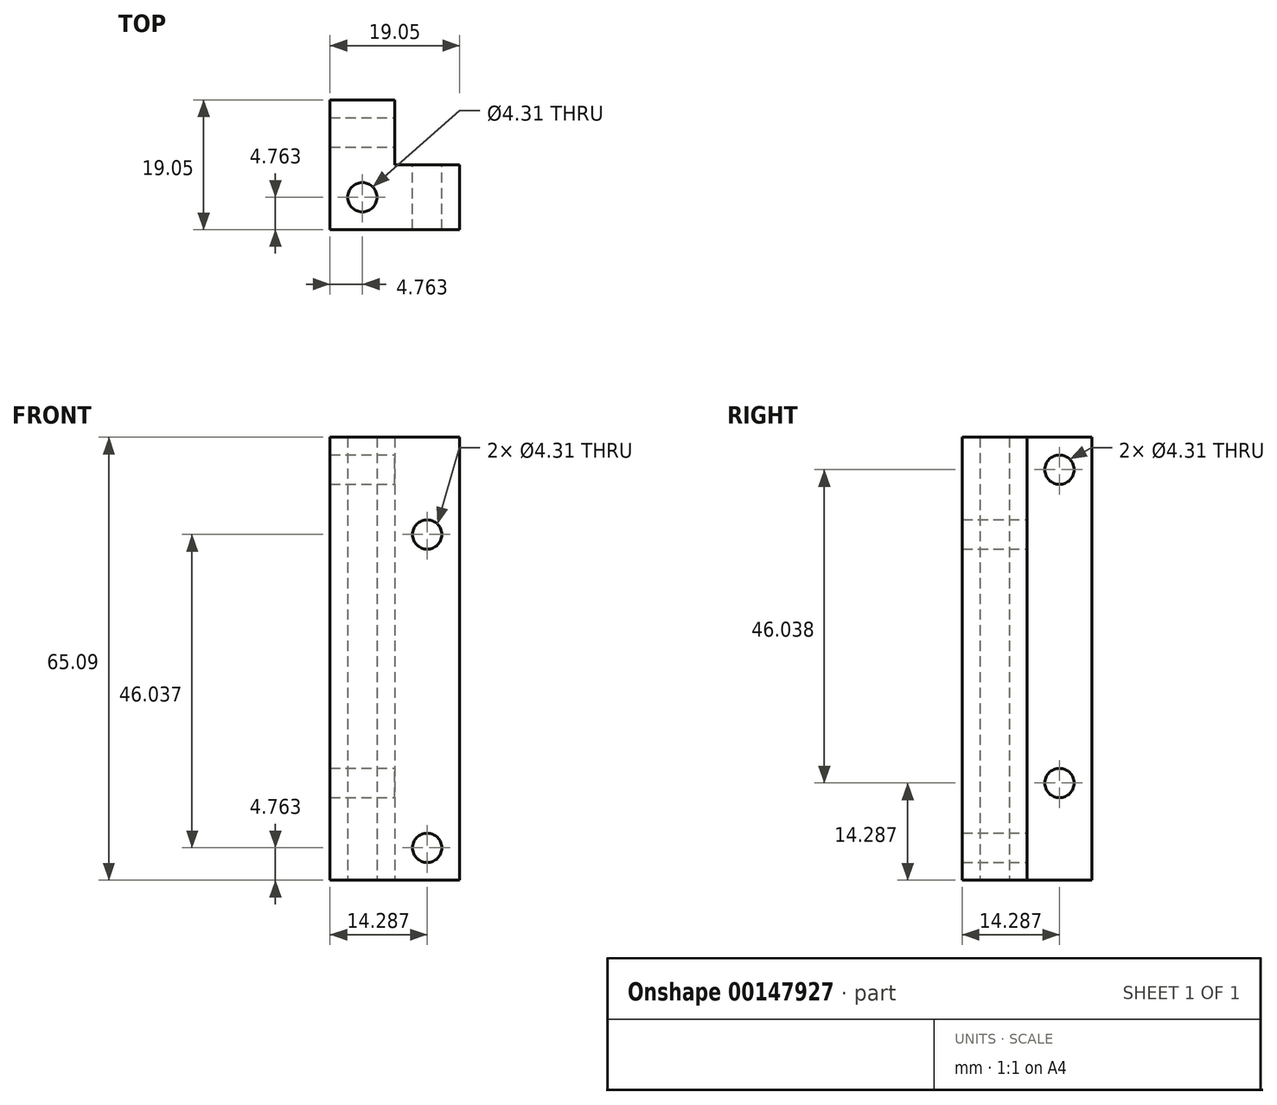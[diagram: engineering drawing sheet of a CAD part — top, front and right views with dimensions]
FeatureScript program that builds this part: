
annotation { "Feature Type Name" : "Feature", "Feature Type Description" : "" }
export const myFeature = defineFeature(function(context is Context, id is Id, definition is map)
    precondition{}
    {
        {
            var Q0;
            Q0=qCreatedBy(makeId("Top.planeOp"),FACE);
            var sketch = newSketch(context, id + "F0", { "sketchPlane" : qUnion([Q0])});
            skLineSegment(sketch, "E0.bottom", {"start": v(0, 0) * mm, "end": v(19.05, 0) * mm});
            skLineSegment(sketch, "E0.left", {"start": v(0, 0) * mm, "end": v(0, 19.05) * mm});
            skLineSegment(sketch, "E1.top", {"start": v(19.05, 9.53) * mm, "end": v(9.52, 9.53) * mm});
            skLineSegment(sketch, "E1.right", {"start": v(9.52, 19.05) * mm, "end": v(9.52, 9.53) * mm});
            skLineSegment(sketch, "E2", {"start": v(0, 19.05) * mm, "end": v(9.52, 19.05) * mm});
            skLineSegment(sketch, "E3", {"start": v(19.05, 9.53) * mm, "end": v(19.05, 0) * mm});
            skLineSegment(sketch, "E4", {"start": v(9.52, 9.53) * mm, "end": v(0, 0) * mm, "construction": true});
            skCircle(sketch, "E5", {"center": v(4.76, 4.76) * mm, "radius": 2.15 * mm});
            skSolve(sketch);
        }
        {
            var Q0;
            Q0=qSketchRegion(id+"F0",true);
            extrude(context, id + "F1", {"entities" : qUnion([Q0]), "depth" : 65.1 * mm});
        }
        {
            var Q0;
            Q0=makeQuery(id+"F1.opExtrude","SWEPT_FACE",FACE,{"disambiguationData":[OSD([sQuery(id+"F0.wireOp",EDGE,"E1.right")])]});
            var sketch = newSketch(context, id + "F2", { "sketchPlane" : qUnion([Q0])});
            skLineSegment(sketch, "E6", {"start": v(14.29, 0) * mm, "end": v(14.29, 14.29) * mm, "construction": true});
            skLineSegment(sketch, "E7", {"start": v(14.29, 65.09) * mm, "end": v(14.29, 60.33) * mm, "construction": true});
            skCircle(sketch, "E8", {"center": v(14.29, 60.33) * mm, "radius": 2.15 * mm});
            skCircle(sketch, "E9", {"center": v(14.29, 14.29) * mm, "radius": 2.15 * mm});
            skSolve(sketch);
        }
        {
            var Q0;
            Q0=qSketchRegion(id+"F2",true);
            var Q1;
            Q1=makeQuery(id+"F1.opExtrude","SWEPT_FACE",FACE,{"disambiguationData":[OSD([sQuery(id+"F0.wireOp",EDGE,"E0.left")])]});
            extrude(context, id + "F3", {"entities" : qUnion([Q0]), "operationType" : NewBodyOperationType.REMOVE, "endBound" : BoundingType.UP_TO_SURFACE, "oppositeDirection" : true, "endBoundEntityFace" : qUnion([Q1]), "depth" : 25.4 * mm});
        }
        {
            var Q0;
            Q0=makeQuery(id+"F1.opExtrude","SWEPT_FACE",FACE,{"disambiguationData":[OSD([sQuery(id+"F0.wireOp",EDGE,"E1.top")])]});
            var sketch = newSketch(context, id + "F4", { "sketchPlane" : qUnion([Q0])});
            skLineSegment(sketch, "E10", {"start": v(-14.29, 65.09) * mm, "end": v(-14.29, 50.8) * mm, "construction": true});
            skLineSegment(sketch, "E11", {"start": v(-14.29, 0) * mm, "end": v(-14.29, 4.76) * mm, "construction": true});
            skCircle(sketch, "E12", {"center": v(-14.29, 50.8) * mm, "radius": 2.15 * mm});
            skCircle(sketch, "E13", {"center": v(-14.29, 4.76) * mm, "radius": 2.15 * mm});
            skSolve(sketch);
        }
        {
            var Q0;
            Q0=qSketchRegion(id+"F4",true);
            var Q1;
            Q1=makeQuery(id+"F1.opExtrude","SWEPT_FACE",FACE,{"disambiguationData":[OSD([sQuery(id+"F0.wireOp",EDGE,"E0.bottom")])]});
            extrude(context, id + "F5", {"entities" : qUnion([Q0]), "operationType" : NewBodyOperationType.REMOVE, "endBound" : BoundingType.UP_TO_SURFACE, "oppositeDirection" : true, "endBoundEntityFace" : qUnion([Q1]), "depth" : 25.4 * mm});
        }
    });
